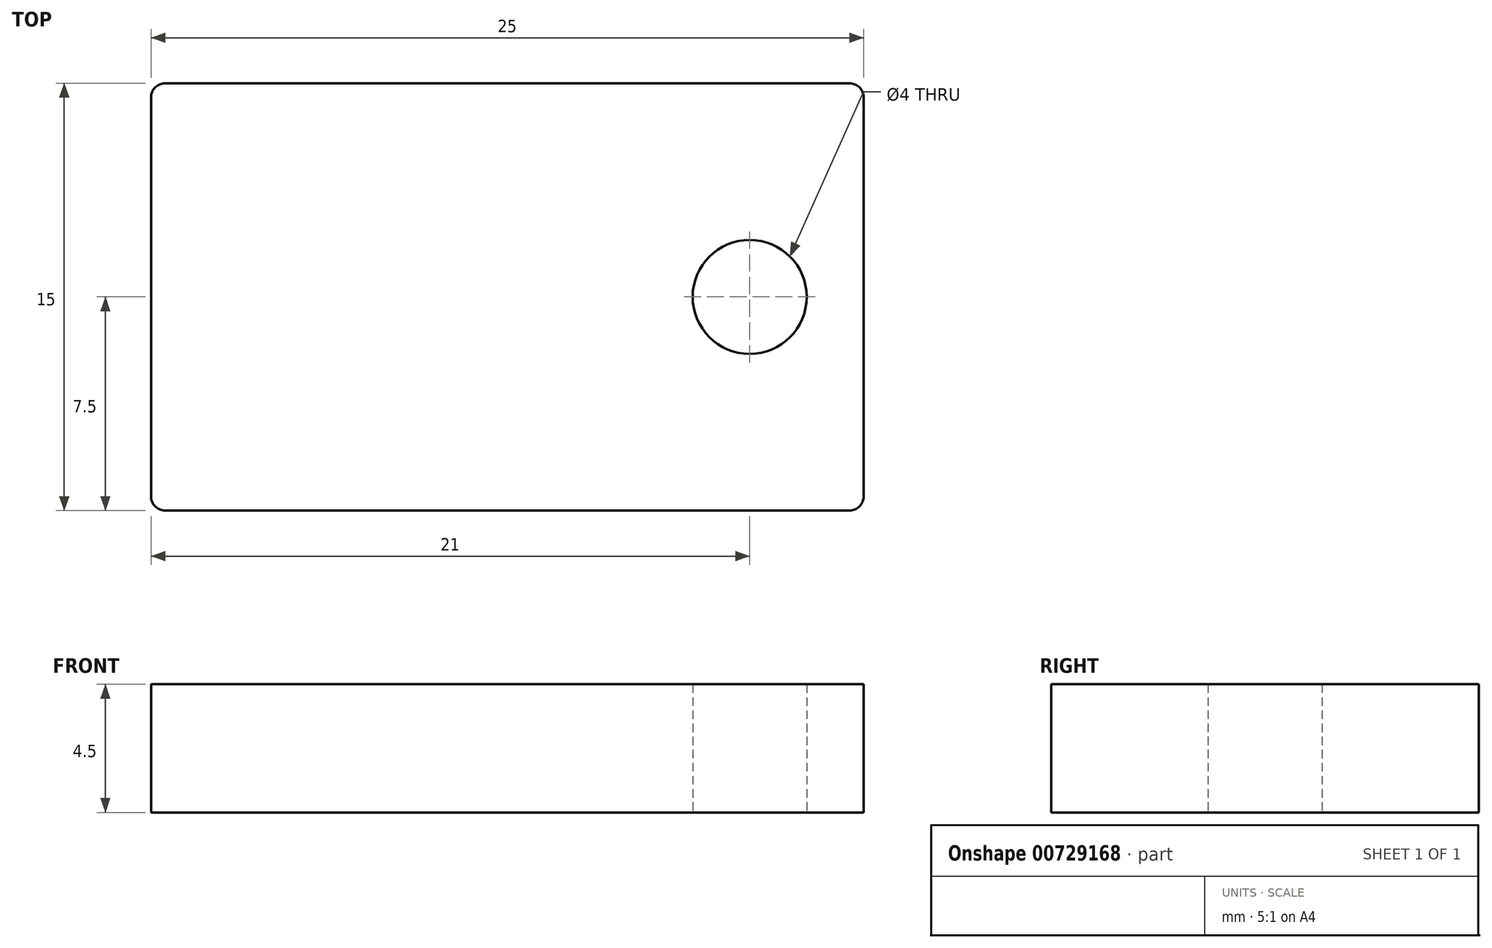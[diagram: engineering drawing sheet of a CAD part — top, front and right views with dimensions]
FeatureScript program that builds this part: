
annotation { "Feature Type Name" : "Feature", "Feature Type Description" : "" }
export const myFeature = defineFeature(function(context is Context, id is Id, definition is map)
    precondition{}
    {
        {
            var Q0;
            Q0=qCreatedBy(makeId("Top.planeOp"),FACE);
            var sketch = newSketch(context, id + "F0", { "sketchPlane" : qUnion([Q0])});
            skLineSegment(sketch, "E0.bottom", {"start": v(12.5, -7.5) * mm, "end": v(-12.5, -7.5) * mm});
            skLineSegment(sketch, "E0.top", {"start": v(12.5, 7.5) * mm, "end": v(-12.5, 7.5) * mm});
            skLineSegment(sketch, "E0.left", {"start": v(12.5, -7.5) * mm, "end": v(12.5, 7.5) * mm});
            skLineSegment(sketch, "E0.right", {"start": v(-12.5, -7.5) * mm, "end": v(-12.5, 7.5) * mm});
            skPoint(sketch, "E0.middle", {"position": v(0, 0) * mm});
            skCircle(sketch, "E1", {"center": v(8.5, 0) * mm, "radius": 2 * mm});
            skPoint(sketch, "E1.centerSnap0", {"position": v(12.5, 0) * mm});
            skSolve(sketch);
        }
        {
            var Q0;
            Q0=qSketchRegion(id+"F0",true);
            extrude(context, id + "F1", {"entities" : qUnion([Q0]), "depth" : 4.5 * mm, "offsetDistance" : 25 * mm});
        }
        {
            var Q0;
            Q0=makeQuery(id+"F1.opExtrude","SWEPT_EDGE",EDGE,{"disambiguationData":[OSD([sQuery(id+"F0.wireOp",EDGE,"E0.top"),sQuery(id+"F0.wireOp",EDGE,"E0.right")])]});
            var Q1;
            Q1=makeQuery(id+"F1.opExtrude","SWEPT_EDGE",EDGE,{"disambiguationData":[OSD([sQuery(id+"F0.wireOp",EDGE,"E0.top"),sQuery(id+"F0.wireOp",EDGE,"E0.left")])]});
            var Q2;
            Q2=makeQuery(id+"F1.opExtrude","SWEPT_EDGE",EDGE,{"disambiguationData":[OSD([sQuery(id+"F0.wireOp",EDGE,"E0.bottom"),sQuery(id+"F0.wireOp",EDGE,"E0.left")])]});
            var Q3;
            Q3=makeQuery(id+"F1.opExtrude","SWEPT_EDGE",EDGE,{"disambiguationData":[OSD([sQuery(id+"F0.wireOp",EDGE,"E0.bottom"),sQuery(id+"F0.wireOp",EDGE,"E0.right")])]});
            fillet(context, id + "F2", {"entities" : qUnion([Q0, Q1, Q2, Q3]), "radius" : 0.5 * mm, "tangentPropagation" : true, "allowEdgeOverflow" : false});
        }
    });
